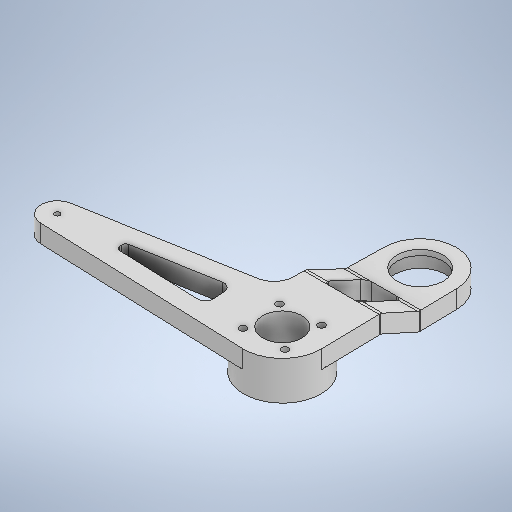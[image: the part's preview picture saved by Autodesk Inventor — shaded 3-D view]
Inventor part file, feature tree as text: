
AUTODESK INVENTOR PART (.ipt)
format: ipt  version: 2025.2 (Build 292293000, 293)  size: 939,008 bytes
history: native  units: mm
features: sketch x12, extrude x11, fillet x5, other x4, projected_geometry x3, loft x2, split x1, move_body x1, boolean_combine x1, mirror x1
ambient origin geometry x8: Origin, YZ Plane, XZ Plane, XY Plane, X Axis, Y Axis, Z Axis, Center Point
bodies: Solid1 (feature_tree), Solid2 (feature_tree), Solid3 (feature_tree)
feature tree (41):
  extrude  "Extrusion1"  Depth=76.5mm
  extrude  "Extrusion2"  Depth=20.0mm
  extrude  "Extrusion3"  Depth=10.0mm TaperAngle=0.0deg
  extrude  "Extrusion4"  Depth=7.0mm TaperAngle=0.0deg
  extrude  "Extrusion5"  TaperAngle=0.0deg  [1 undecoded]
  fillet  "Fillet3"  Radius=117.0mm
  sketch  "Sketch6"  dims[d27=10.0mm d28=0.0mm d31=15.009832mm]
  split  "Split1"
  move_body  "Move Body1"
  extrude  "Extrusion6"  Depth=3.0mm
  sketch  "Sketch8"  dims[d33=10.75mm d34=23.6mm]
  sketch  "Sketch9"  dims[d35=40.0mm d40=0.0mm d41=10.0mm d42=0.0mm]
  extrude  "Extrusion7"  Depth=10.0mm
  extrude  "Extrusion8"  Depth=23.6mm
  loft  "Loft2"
  loft  "Loft3"
  boolean_combine  "Combine2"
  fillet  "Fillet6"  Radius=20.0mm
  fillet  "Fillet7"  Radius=1.0mm
  extrude  "Extrusion9"  TaperAngle=0.0deg  [1 undecoded]
  fillet  "Fillet8"  [1 undecoded]
  fillet  "Fillet9"  Radius=3.0mm
  extrude  "Extrusion10"  Depth=4.5mm
  extrude  "Extrusion11"  TaperAngle=0.0deg  [1 undecoded]
  mirror  "Mirror1"
  sketch  "Sketch1"  dims[d0=40.0mm d3=76.5mm]
  sketch  "Sketch2"  dims[d6=10.0mm d7=0.0mm d8=11.5mm d9=0.0mm]
  sketch  "Sketch3"  dims[d10=28.07mm d12=7.0mm d13=0.0mm]
  sketch  "Sketch4"  dims[d14=1.3mm d15=0.0mm d16=0.0mm d17=117.0mm]
  sketch  "Sketch5"  dims[d19=3.0mm d21=18.0mm]
  projected_geometry  "Projected Loop1"
  projected_geometry  "Projected Loop2"
  projected_geometry  "Projected Loop3"
  other  "Edges3"
  other  "Edges4"
  other  "Edges5"
  other  "Edges6"
  sketch  "Sketch10"  dims[d43=0.0mm d44=0.0mm d49=20.0mm d51=20.0mm d53=1.0mm d54=0.0mm]
  sketch  "Sketch11"  dims[d55=1.0mm d56=0.0mm d66=0.0mm d67=90.0deg d68=0.0mm d69=90.0deg]
  sketch  "Sketch12"  dims[d70=0.0mm d71=90.0deg d72=0.0mm d73=90.0deg d75=3.0mm d76=4.5mm d79=0.0mm d80=0.0mm d83=4.5mm d84=2.0mm d85=21.7mm d86=0.0mm d87=0.0mm d88=30.9mm d90=4.0mm d91=40.0mm d93=360.0deg d95=0.0mm d96=0.0mm d97=7.15585mm d36=0.5mm d37=0.872665mm d38=0.5mm d39=0.872665mm d77=0.0mm d78=0.0mm]
  sketch  "Sketch Circular Pattern1"  dims[d4=1.5mm d5=20.0mm]
note: 4 required parameter values undecoded (feature->parameter linkage not recoverable at this tier; creation-order binding heuristic only, values carry confidence <= 0.55)
